# Revit family: IS_CeraplusSafe_A2940_BIM_DE
name_source: partatom
category: Plumbing Fixtures
units: mm (PartAtom-declared; Revit-internal decimal feet)

## family parameters
Cut with Voids When Loaded = No
Host = Face
Maintain Annotation Orientation = No
OmniClass Number = 23.45.55.17
OmniClass Title = Mixing Faucets
Part Type = Normal
Room Calculation Point = No
Round Connector Dimension = Use Diameter
Shared = Yes

## types (1)
- A7940AA - CERAPLUS SAFE SHRSYS TH EXPSD
    Accessories = https://www.idealstandard.de
    AreaUnits = Square millimeters
    Assembly Code = C1030200
    BIMObjectName = IS_IdealStandard_ShowerSystem_CeraplusSafe_A7940
    BIMobject category = Showers
    BREEAMApproved = No
    BarCode = 4015413357166
    Brand = Ideal Standard
    Brand url = https://www.idealstandard.de
    CWFU = 0
    Color = Chrome
    ConnectionType = Plumbing
    Cost = 0 $
    CurrencyUnit = Euro
    CurrentRevision = 1
    Date of publishing = 2023-10-06
    Default Elevation = 800 mm  [stored 2.62467 ft]
    Description = Ceraplus Safe Shower System, Thermal Disinfection, Cool Body, Bar Hand Shower (8 l/min), Head Shower (12 l/min), S-couplings
Ceraplus Safe Shower System, Thermal Disinfection, Cool Body, Bar Hand Shower (8 l/min), Head Shower (12 l/min), S-couplings
Ceraplus Safe Shower System, Thermal Disinfection, Cool Body, Bar Hand Shower (8 l/min), Head Shower (12 l/min), S-couplings
Ceraplus Safe Shower System, Thermal Disinfection, Cool Body, Bar Hand Shower (8 l/min), Head Shower (12 l/min), S-couplings
    DurationUnit = year
    ECA = No
    EPD = https://www.idealstandard.de
    Edition number = 1
    ExpectedLife = 30
    FaucetFunction = MIXED
    FaucetOperation = LEVERHANDLE
    FaucetType = PILLAR
    Features = Ceraplus Safe Shower System, Thermal Disinfection, Cool Body, Bar Hand Shower (8 l/min), Head Shower (12 l/min), S-couplings, Metal Handles with Red&Blue Markings, IdealFlex Shower Hose (1750mm)
    Finish = Chrome
    FlowRate = 8 lpm hand & 12 lpm head shower
    GTIN code = 4015413357166
    HWFU = 0
    Help = https://www.idealstandard.co.uk
    IfcExportAs = IfcValveType
    IfcExportType = FAUCET
    InstallationInstructions = https://www.idealstandard.de
    LinearUnits = millimeters
    Manufacturer = https://www.idealstandard.de
    Manufacturer name = Ideal Standard
    ManufacturerURL = https://www.idealstandard.de
    Material = Brass
    Material main = Brass
    Model = A7940AA
    ModelNumber = A7940AA
    ModelReference = Ceraplus Safe Shower System, Thermal Disinfection, Cool Body, Bar Hand Shower (8 l/min), Head Shower (12 l/min), S-couplings
Ceraplus Safe Shower System, Thermal Disinfection, Cool Body, Bar Hand Shower (8 l/min), Head Shower (12 l/min), S-couplings
Ceraplus Safe Shower System, Thermal Disinfection, Cool Body, Bar Hand Shower (8 l/min), Head Shower (12 l/min), S-couplings
Ceraplus Safe Shower System, Thermal Disinfection, Cool Body, Bar Hand Shower (8 l/min), Head Shower (12 l/min), S-couplings
    NBSReference = 45-35-70/???
    Name = ShowerSystem_CeraplusSafe_A7940_Idealstandard
    NettWeight = 5.71 Kg
    NominalHeight = 1191 mm
    NominalLength = 586 mm
    NominalWidth = 296 mm  [stored 0.971129 ft]
    OmniClass Code = 23.45.55.17
    OmniClass Description = Mixing Faucets
    Product SKU = A7940AA
    Product data url = https://www.idealstandard.de
    Product family = CeraplusSafe
    Product name = ShowerSystem_CeraplusSafe_A7940_Idealstandard
    Product url = https://www.idealstandard.de
    ProductInformation = https://www.idealstandard.de
    Revision = 1
    Shape = Sculptured / Cylindical
    Size = 296 x 586 x 1191 mm
    Space = Internal
    SpareParts = https://www.idealstandard.de
    TMV3 = Yes
    Technical description = https://www.idealstandard.de
    TestPressure = 10 Bar
    URL = https://www.idealstandard.de
    Uniclass2 = Pr_40_20_87_98
    Version = 1
    VolumeUnits = Litres
    WFU = 0
    WRAS = Yes
    WarrantyDescription = Manufacturers Warranty
    WarrantyDurationParts = 5
    WarrantyDurationUnit = year
    WarrantyGuarantorParts = https://www.idealstandard.de
    WaterEfficientProduct = No
    WorkingPressure = 3 Bar
    Youtube clip = https://www.youtube.com

note: [stored X ft] marks values corroborated as IEEE doubles in the binary element streams (Revit-internal decimal feet)

## geometry (parser evidence)
native form markers: Sweep x3
no freeform markers — native parametric forms only
